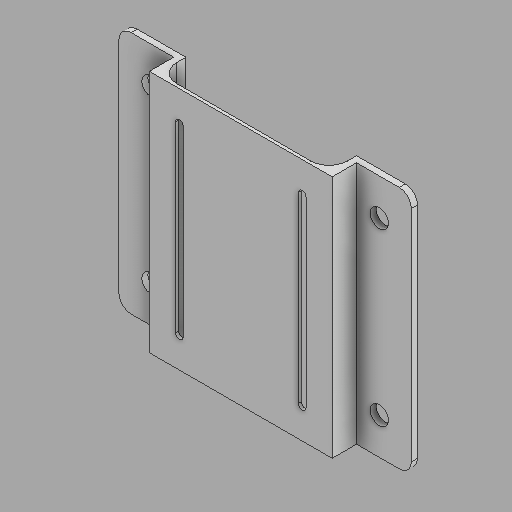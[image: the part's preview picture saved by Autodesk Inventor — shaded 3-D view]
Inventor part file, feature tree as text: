
AUTODESK INVENTOR PART (.ipt)
format: ipt  version: 2025.2 (Build 292293000, 293)  size: 167,424 bytes
history: native  units: in
note: dims shown in document units (in); Inventor stores cm internally (conversion verified against a paired STEP export)
features: sketch x5, extrude x4, fillet x2, hole x1
ambient origin geometry x8: Origin, YZ Plane, XZ Plane, XY Plane, X Axis, Y Axis, Z Axis, Center Point
bodies: Solid1 (feature_tree)
feature tree (12):
  extrude  "Extrusion1"  Depth=2.5in
  hole  "Hole1"  [1 undecoded]
  extrude  "Extrusion2"  Depth=1.875in
  extrude  "Extrusion3"  Depth=0.0312in
  extrude  "Extrusion4"  Depth=0.0625in
  fillet  "Fillet1"  Radius=0.0625in
  fillet  "Fillet2"  [1 undecoded]
  sketch  "Sketch1"  dims[d0=3.0in d1=2.5in]
  sketch  "Sketch2"  dims[d2=0.0625in d3=0.0in d4=2.3437in]
  sketch  "Sketch4"  dims[d5=0.375in]
  sketch  "Sketch5"  dims[d6=0.188in d7=0.75in d8=0.375in d9=0.25in d10=0.5635in d11=1.0in d12=0.8108in d13=1.875in]
  sketch  "Sketch6"  dims[d14=0.25in d15=0.0in d16=0.0312in d17=0.0625in d18=0.0625in d19=0.0in d20=0.0in d21=1.2598in d22=0.0787in d23=0.3125in d24=0.0in d25=0.0in d26=0.125in d30=0.1875in]
note: 2 required parameter values undecoded (feature->parameter linkage not recoverable at this tier; creation-order binding heuristic only, values carry confidence <= 0.55)
